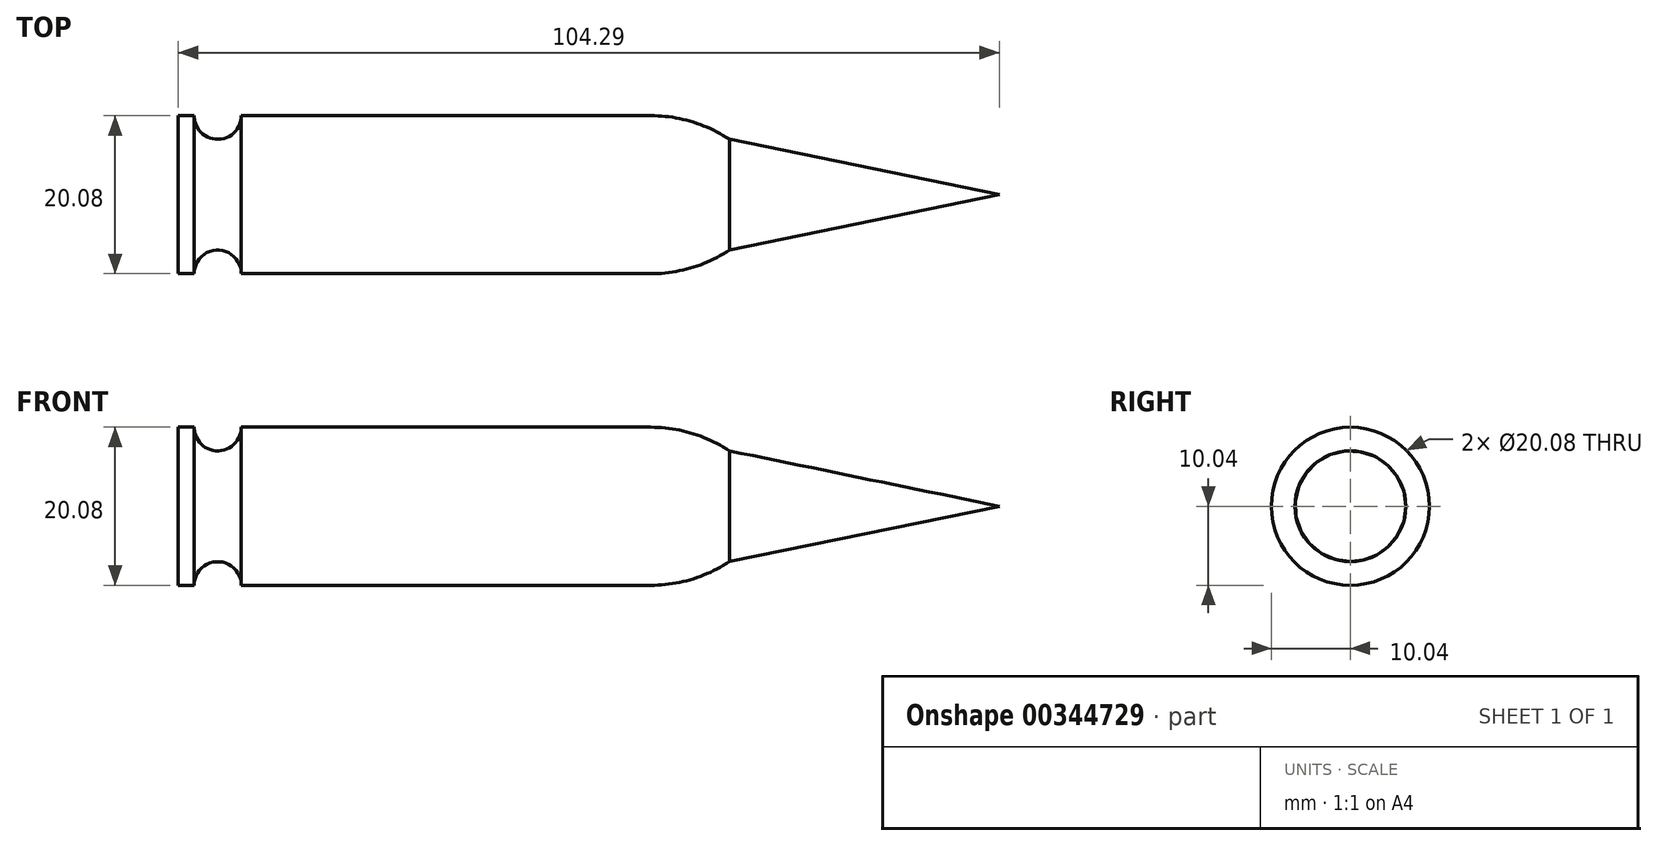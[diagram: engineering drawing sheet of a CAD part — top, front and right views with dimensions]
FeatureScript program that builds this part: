
annotation { "Feature Type Name" : "Feature", "Feature Type Description" : "" }
export const myFeature = defineFeature(function(context is Context, id is Id, definition is map)
    precondition{}
    {
        {
            var Q0;
            Q0=qCreatedBy(makeId("Front.planeOp"),FACE);
            var sketch = newSketch(context, id + "F0", { "sketchPlane" : qUnion([Q0])});
            skPoint(sketch, "E0", {"position": v(0, 10.04) * mm});
            skLineSegment(sketch, "E1", {"start": v(0, 10.04) * mm, "end": v(2, 10.04) * mm});
            skPoint(sketch, "E2", {"position": v(2, 10.04) * mm});
            skPoint(sketch, "E3", {"position": v(8, 10.04) * mm});
            skPoint(sketch, "E4", {"position": v(5, 10.04) * mm});
            skArc(sketch, "E5", {"start": v(2, 10.04) * mm, "mid": v(5, 7.04) * mm, "end": v(8, 10.04) * mm});
            skPoint(sketch, "E5.third.point", {"position": v(5, 7.04) * mm});
            skLineSegment(sketch, "E6.trimOffspring", {"start": v(8, 10.04) * mm, "end": v(10, 10.04) * mm});
            skPoint(sketch, "E7", {"position": v(60, 10.04) * mm});
            skLineSegment(sketch, "E8", {"start": v(10, 10.04) * mm, "end": v(60, 10.04) * mm});
            skPoint(sketch, "E9", {"position": v(70, 10.04) * mm});
            skPoint(sketch, "E10", {"position": v(70, 7.04) * mm});
            skArc(sketch, "E11", {"start": v(70, 7.04) * mm, "mid": v(65.23, 9.27) * mm, "end": v(60, 10.04) * mm});
            skLineSegment(sketch, "E12", {"start": v(70, 7.04) * mm, "end": v(104.3, 0) * mm});
            skLineSegment(sketch, "E13", {"start": v(0, 10.04) * mm, "end": v(0, 0) * mm});
            skSolve(sketch);
        }
        {
            var Q0;
            Q0=qCreatedBy(makeId("Front.planeOp"),FACE);
            var sketch = newSketch(context, id + "F1", { "sketchPlane" : qUnion([Q0])});
            skLineSegment(sketch, "E14", {"start": v(-65.24, 0) * mm, "end": v(-28.7, 0) * mm});
            skSolve(sketch);
        }
        {
            var Q0;
            Q0 = qSketchRegion(id + "F0", true);
            var Q1;
            Q1 = qConstructionFilter(qBodyType(qCreatedBy(id + "F0" ,EDGE), BodyType.WIRE), ConstructionObject.NO);
            var Q2;
            Q2=sQuery(id+"F1.wireOp",EDGE,"E14");
            revolve(context, id + "F2", {"bodyType" : ToolBodyType.SURFACE, "entities" : qUnion([Q0]), "surfaceEntities" : qUnion([Q1]), "axis" : qUnion([Q2]), "revolveType" : RevolveType.FULL});
        }
    });
